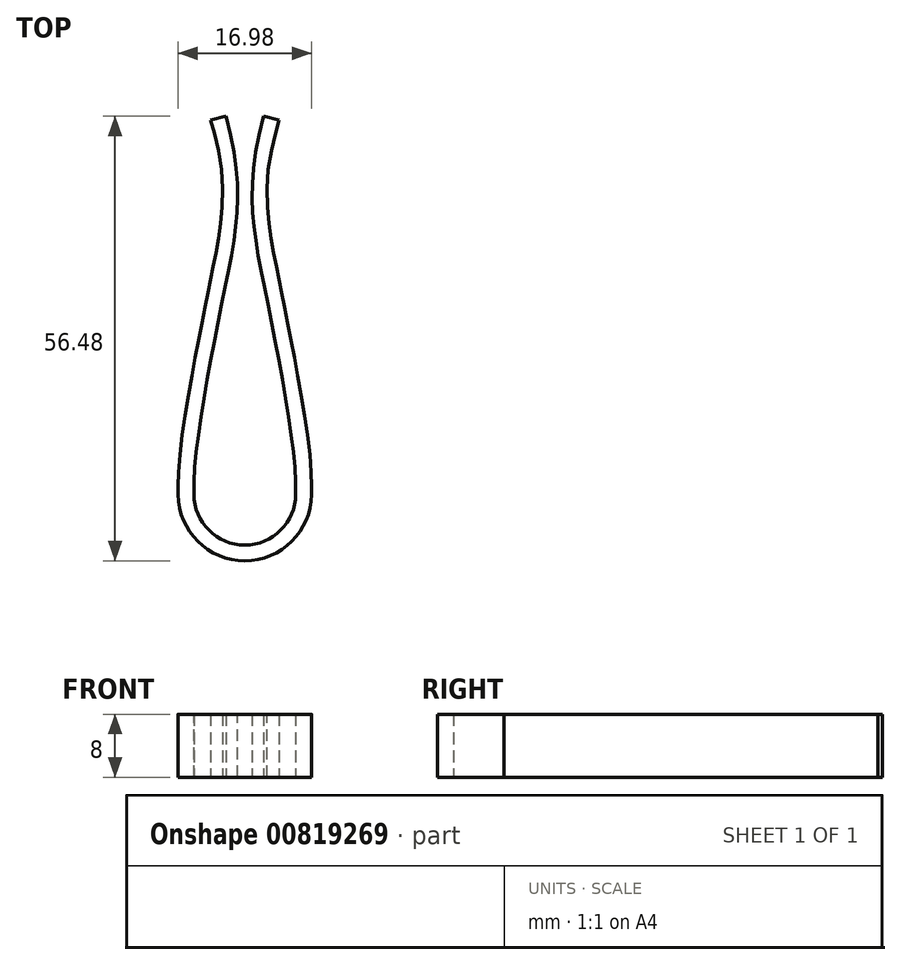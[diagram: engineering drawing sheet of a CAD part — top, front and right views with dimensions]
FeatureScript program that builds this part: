
annotation { "Feature Type Name" : "Feature", "Feature Type Description" : "" }
export const myFeature = defineFeature(function(context is Context, id is Id, definition is map)
    precondition{}
    {
        {
            var Q0;
            Q0=qCreatedBy(makeId("Top.planeOp"),FACE);
            var sketch = newSketch(context, id + "F0", { "sketchPlane" : qUnion([Q0])});
            skLineSegment(sketch, "E0", {"start": v(0, 0) * mm, "end": v(0, 48.02) * mm, "construction": true});
            skLineSegment(sketch, "E1", {"start": v(0, 48.02) * mm, "end": v(-2.4, 48.02) * mm, "construction": true});
            skLineSegment(sketch, "E2", {"start": v(-2.4, 48.02) * mm, "end": v(7.78, 48.02) * mm, "construction": true});
            skArc(sketch, "E3", {"start": v(-6.46, 0) * mm, "mid": v(0, -6.46) * mm, "end": v(6.46, 0) * mm});
            skFitSpline(sketch, "E4", {"points": [v(-2.4, 48.02) * mm, v(-2.4, 26.72) * mm, v(-6.46, 0) * mm], "startDerivative": vector(15.37, -57.03) * mm, "endDerivative": vector(1.15, -33.7) * mm});
            skFitSpline(sketch, "E5.MirrorCS", {"points": [v(2.4, 48.02) * mm, v(2.4, 26.72) * mm, v(6.46, 0) * mm], "startDerivative": vector(-15.37, -57.03) * mm, "endDerivative": vector(-1.15, -33.7) * mm});
            skFitSpline(sketch, "E6.0", {"points": [v(4.34, 47.5) * mm, v(3.72, 45.2) * mm, v(2.95, 41.24) * mm, v(2.85, 37.16) * mm, v(3.15, 33.94) * mm, v(3.53, 31.42) * mm, v(3.96, 29.16) * mm, v(4.35, 27.2) * mm, v(4.77, 25.13) * mm, v(5.32, 22.38) * mm, v(6, 18.92) * mm, v(6.67, 15.38) * mm, v(7.48, 10.7) * mm, v(8.13, 6.25) * mm, v(8.45, 2.4) * mm, v(8.48, 0.71) * mm, v(8.46, -0.07) * mm]});
            skArc(sketch, "E6.1", {"start": v(-8.46, -0.04) * mm, "mid": v(0, -8.46) * mm, "end": v(8.46, -0.04) * mm});
            skFitSpline(sketch, "E6.2", {"points": [v(-4.34, 47.5) * mm, v(-3.72, 45.2) * mm, v(-2.95, 41.24) * mm, v(-2.85, 37.16) * mm, v(-3.15, 33.94) * mm, v(-3.53, 31.42) * mm, v(-3.96, 29.16) * mm, v(-4.35, 27.2) * mm, v(-4.77, 25.13) * mm, v(-5.32, 22.38) * mm, v(-6, 18.92) * mm, v(-6.67, 15.38) * mm, v(-7.48, 10.7) * mm, v(-8.13, 6.25) * mm, v(-8.45, 2.4) * mm, v(-8.48, 0.71) * mm, v(-8.46, -0.07) * mm]});
            skLineSegment(sketch, "E7", {"start": v(-4.34, 47.5) * mm, "end": v(-2.4, 48.02) * mm});
            skLineSegment(sketch, "E8", {"start": v(2.4, 48.02) * mm, "end": v(4.34, 47.5) * mm});
            skSolve(sketch);
        }
        {
            var Q0;
            Q0 = qSketchRegion(id + "F0", true);
            extrude(context, id + "F1", {"entities" : qUnion([Q0]), "depth" : 8 * mm, "offsetDistance" : 25.4 * mm});
        }
    });
